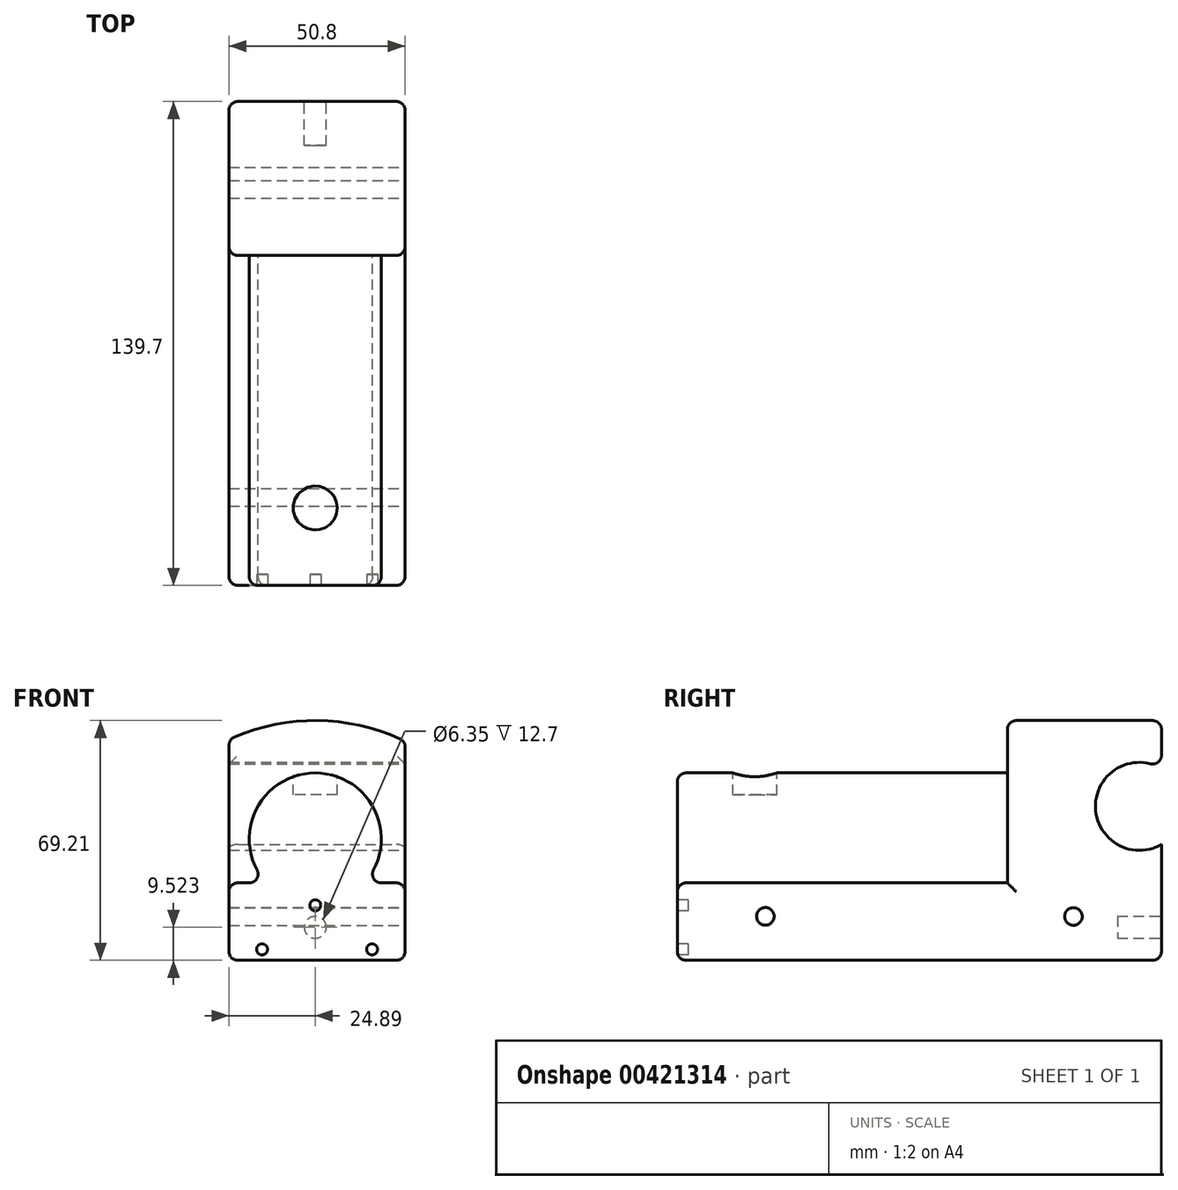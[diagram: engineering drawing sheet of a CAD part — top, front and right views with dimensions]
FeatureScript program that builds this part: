
annotation { "Feature Type Name" : "Feature", "Feature Type Description" : "" }
export const myFeature = defineFeature(function(context is Context, id is Id, definition is map)
    precondition{}
    {
        {
            var Q0;
            Q0=qCreatedBy(makeId("Front.planeOp"),FACE);
            var sketch = newSketch(context, id + "F0", { "sketchPlane" : qUnion([Q0])});
            skLineSegment(sketch, "E0.bottom", {"start": v(-24.89, 0) * mm, "end": v(-14.2, 0) * mm});
            skLineSegment(sketch, "E0.top", {"start": v(-24.89, -22.35) * mm, "end": v(25.91, -22.35) * mm});
            skLineSegment(sketch, "E0.left", {"start": v(-24.89, 0) * mm, "end": v(-24.89, -22.35) * mm});
            skLineSegment(sketch, "E0.right", {"start": v(25.91, 0) * mm, "end": v(25.91, -22.35) * mm});
            skArc(sketch, "E1", {"start": v(14.2, 0) * mm, "mid": v(0, 31.75) * mm, "end": v(-14.2, 0) * mm});
            skLineSegment(sketch, "E2.trimOffspring", {"start": v(14.2, 0) * mm, "end": v(25.91, 0) * mm});
            skSolve(sketch);
        }
        {
            var Q0;
            Q0=makeQuery(id+"F0.imprint","IMPRINT",FACE,{"disambiguationData":[TD([[makeQuery(id+"F0.imprint","IMPRINT",EDGE,{"derivedFrom":sQuery(id+"F0.wireOp",EDGE,"E0.bottom")}),-1.0]])]});
            extrude(context, id + "F1", {"entities" : qUnion([Q0]), "depth" : 95.25 * mm});
        }
        {
            var Q0;
            Q0=makeQuery(id+"F1.opExtrude","CAP_FACE",FACE,{"disambiguationData":[OSD([sQuery(id+"F0.wireOp",EDGE,"E0.bottom"),sQuery(id+"F0.wireOp",EDGE,"E0.top"),sQuery(id+"F0.wireOp",EDGE,"E0.left"),sQuery(id+"F0.wireOp",EDGE,"E0.right"),sQuery(id+"F0.wireOp",EDGE,"E1"),sQuery(id+"F0.wireOp",EDGE,"E2.trimOffspring")])],"isStart":true});
            var sketch = newSketch(context, id + "F2", { "sketchPlane" : qUnion([Q0])});
            skArc(sketch, "E3", {"start": v(24.89, 41.43) * mm, "mid": v(-0.57, 46.86) * mm, "end": v(-25.91, 40.95) * mm});
            skLineSegment(sketch, "E4", {"start": v(-25.91, 0) * mm, "end": v(-25.91, 40.95) * mm});
            skLineSegment(sketch, "E5", {"start": v(-25.91, 40.95) * mm, "end": v(-25.91, 40.95) * mm});
            skLineSegment(sketch, "E6", {"start": v(24.89, 0) * mm, "end": v(24.89, 41.43) * mm});
            skSolve(sketch);
        }
        {
            var Q0;
            Q0=makeQuery(id+"F2.imprint","IMPRINT",FACE,{"disambiguationData":[TD([[makeQuery(id+"F2.imprint","IMPRINT",EDGE,{"derivedFrom":sQuery(id+"F2.wireOp",EDGE,"E3")}),1.0]])]});
            var Q1;
            Q1=makeQuery(id+"F2.imprint","IMPRINT",FACE,{"disambiguationData":[TD([[makeQuery(id+"F2.imprint","IMPRINT",EDGE,{"derivedFrom":makeQuery(id+"F1.opExtrude","CAP_EDGE",EDGE,{"disambiguationData":[OSD([sQuery(id+"F0.wireOp",EDGE,"E0.bottom")])],"isStart":true})}),1.0]])]});
            extrude(context, id + "F3", {"entities" : qUnion([Q0, Q1]), "operationType" : NewBodyOperationType.ADD, "depth" : 44.45 * mm});
        }
        {
            var Q0;
            {var subQ0=sQuery(id+"F0.wireOp",EDGE,"E0.right");Q0=makeQuery(id+"F3.boolean.opBoolean","MERGE",FACE,{"derivedFrom":[makeQuery(id+"F1.opExtrude","SWEPT_FACE",FACE,{"disambiguationData":[OSD([subQ0])]}),makeQuery(id+"F3.opExtrude","SWEPT_FACE",FACE,{"disambiguationData":[OSD([subQ0,sQuery(id+"F2.wireOp",EDGE,"E4")])]})]});}
            var sketch = newSketch(context, id + "F4", { "sketchPlane" : qUnion([Q0])});
            skArc(sketch, "E7", {"start": v(44.45, 33.1) * mm, "mid": v(25.4, 22.1) * mm, "end": v(44.45, 11.1) * mm});
            skLineSegment(sketch, "E8", {"start": v(44.45, 33.1) * mm, "end": v(44.45, 11.1) * mm});
            skPoint(sketch, "E8.endSnap0", {"position": v(44.45, 9.3) * mm});
            skSolve(sketch);
        }
        {
            var Q0;
            Q0=makeQuery(id+"F4.imprint","IMPRINT",FACE,{"disambiguationData":[TD([[makeQuery(id+"F4.imprint","IMPRINT",EDGE,{"derivedFrom":sQuery(id+"F4.wireOp",EDGE,"E7")}),1.0]])]});
            extrude(context, id + "F5", {"entities" : qUnion([Q0]), "operationType" : NewBodyOperationType.REMOVE, "oppositeDirection" : true, "depth" : 50.8 * mm});
        }
        {
            var Q0;
            Q0=makeQuery(id+"F1.opExtrude","CAP_FACE",FACE,{"disambiguationData":[OSD([sQuery(id+"F0.wireOp",EDGE,"E0.bottom"),sQuery(id+"F0.wireOp",EDGE,"E0.top"),sQuery(id+"F0.wireOp",EDGE,"E0.left"),sQuery(id+"F0.wireOp",EDGE,"E0.right"),sQuery(id+"F0.wireOp",EDGE,"E1"),sQuery(id+"F0.wireOp",EDGE,"E2.trimOffspring")])],"isStart":false});
            var sketch = newSketch(context, id + "F6", { "sketchPlane" : qUnion([Q0])});
            skCircle(sketch, "E9", {"center": v(-15.36, -19.18) * mm, "radius": 1.59 * mm});
            skCircle(sketch, "E10", {"center": v(0, -6.48) * mm, "radius": 1.59 * mm});
            skCircle(sketch, "E11", {"center": v(16.39, -19.18) * mm, "radius": 1.59 * mm});
            skLineSegment(sketch, "E12.0", {"start": v(-24.89, -22.35) * mm, "end": v(25.91, -22.35) * mm});
            skSolve(sketch);
        }
        {
            var Q0;
            Q0=makeQuery(id+"F6.imprint","IMPRINT",FACE,{"disambiguationData":[TD([[makeQuery(id+"F6.imprint","IMPRINT",EDGE,{"derivedFrom":sQuery(id+"F6.wireOp",EDGE,"E10")}),1.0]])]});
            var Q1;
            Q1=makeQuery(id+"F6.imprint","IMPRINT",FACE,{"disambiguationData":[TD([[makeQuery(id+"F6.imprint","IMPRINT",EDGE,{"derivedFrom":sQuery(id+"F6.wireOp",EDGE,"E9")}),1.0]])]});
            var Q2;
            Q2=makeQuery(id+"F6.imprint","IMPRINT",FACE,{"disambiguationData":[TD([[makeQuery(id+"F6.imprint","IMPRINT",EDGE,{"derivedFrom":sQuery(id+"F6.wireOp",EDGE,"E11")}),1.0]])]});
            extrude(context, id + "F7", {"entities" : qUnion([Q0, Q1, Q2]), "operationType" : NewBodyOperationType.REMOVE, "oppositeDirection" : true, "depth" : 3.17 * mm});
        }
        {
            var Q0;
            {var subQ0=sQuery(id+"F0.wireOp",EDGE,"E0.right");Q0=makeQuery(id+"F3.boolean.opBoolean","MERGE",FACE,{"derivedFrom":[makeQuery(id+"F1.opExtrude","SWEPT_FACE",FACE,{"disambiguationData":[OSD([subQ0])]}),makeQuery(id+"F3.opExtrude","SWEPT_FACE",FACE,{"disambiguationData":[OSD([subQ0,sQuery(id+"F2.wireOp",EDGE,"E4")])]})]});}
            var sketch = newSketch(context, id + "F8", { "sketchPlane" : qUnion([Q0])});
            skPoint(sketch, "E13", {"position": v(-69.85, -9.65) * mm});
            skPoint(sketch, "E14", {"position": v(19.05, -9.7) * mm});
            skSolve(sketch);
        }
        {
            var Q0;
            Q0=sQuery(id+"F8.wireOp",VERTEX,"E13");
            var Q1;
            Q1=sQuery(id+"F8.wireOp",VERTEX,"E14");
            var Q2;
            Q2=makeQuery(id+"F1.opExtrude","SWEPT_BODY",BODY,{"disambiguationData":[OSD([sQuery(id+"F0.wireOp",EDGE,"E0.bottom"),sQuery(id+"F0.wireOp",EDGE,"E0.top"),sQuery(id+"F0.wireOp",EDGE,"E0.left"),sQuery(id+"F0.wireOp",EDGE,"E0.right"),sQuery(id+"F0.wireOp",EDGE,"E1"),sQuery(id+"F0.wireOp",EDGE,"E2.trimOffspring")])]});
            hole(context, id + "F9", {"style" : HoleStyle.SIMPLE, "endStyle" : HoleEndStyle.THROUGH, "standardTappedOrClearance" : lookupTablePath({ "standard" : "ANSI", "fit" : "Normal (ASME)", "engagement" : "75%", "pitch" : "20 tpi", "size" : "1/4", "type" : "Tapped" }), "standardBlindInLast" : lookupTablePath({ "fit" : "Free", "standard" : "ANSI", "engagement" : "75%", "pitch" : "20 tpi", "size" : "1/4", "type" : "Tapped" }), "holeDiameter" : 5.1 * mm, "showTappedDepth" : true, "tappedDepth" : 50.8 * mm, "tapClearance" : 3, "locations" : qUnion([Q0, Q1]), "scope" : qUnion([Q2]), "majorDiameter" : 6.35 * mm});
        }
        {
            var Q0;
            Q0=qCreatedBy(makeId("Top.planeOp"),FACE);
            cPlane(context, id + "F10", {"entities" : qUnion([Q0]), "cplaneType" : CPlaneType.OFFSET, "offset" : 31.75 * mm, "width" : 152.4 * mm, "height" : 152.4 * mm});
        }
        {
            var Q0;
            Q0=qCreatedBy(id+"F10.planeOp",FACE);
            var sketch = newSketch(context, id + "F11", { "sketchPlane" : qUnion([Q0])});
            skCircle(sketch, "E15", {"center": v(0, -72.9) * mm, "radius": 6.35 * mm});
            skSolve(sketch);
        }
        {
            var Q0;
            Q0=makeQuery(id+"F11.imprint","IMPRINT",FACE,{"disambiguationData":[TD([[makeQuery(id+"F11.imprint","IMPRINT",EDGE,{"derivedFrom":sQuery(id+"F11.wireOp",EDGE,"E15")}),1.0]])]});
            extrude(context, id + "F12", {"entities" : qUnion([Q0]), "operationType" : NewBodyOperationType.REMOVE, "oppositeDirection" : true, "depth" : 6.35 * mm});
        }
        {
            var Q0;
            {var subQ0=sQuery(id+"F2.wireOp",EDGE,"E4");var subQ1=sQuery(id+"F0.wireOp",EDGE,"E0.right");var subQ2=sQuery(id+"F0.wireOp",EDGE,"E0.left");var subQ3=sQuery(id+"F2.wireOp",EDGE,"E6");var subQ4=sQuery(id+"F0.wireOp",EDGE,"E0.top");Q0=makeQuery(id+"F5.boolean.opBoolean","SPLIT",FACE,{"disambiguationData":[TD([makeQuery(id+"F1.opExtrude","SWEPT_FACE",FACE,{"disambiguationData":[OSD([subQ4])]})])],"derivedFrom":makeQuery(id+"F3.opExtrude","CAP_FACE",FACE,{"disambiguationData":[OSD([subQ4,subQ2,subQ1,sQuery(id+"F2.wireOp",EDGE,"E3"),subQ0,subQ3])],"isStart":false})});}
            var sketch = newSketch(context, id + "F13", { "sketchPlane" : qUnion([Q0])});
            skCircle(sketch, "E16", {"center": v(0, -12.83) * mm, "radius": 3.18 * mm});
            skSolve(sketch);
        }
        {
            var Q0;
            Q0=makeQuery(id+"F13.imprint","IMPRINT",FACE,{"disambiguationData":[TD([[makeQuery(id+"F13.imprint","IMPRINT",EDGE,{"derivedFrom":sQuery(id+"F13.wireOp",EDGE,"E16")}),1.0]])]});
            extrude(context, id + "F14", {"entities" : qUnion([Q0]), "operationType" : NewBodyOperationType.REMOVE, "oppositeDirection" : true, "offsetDistance" : 25.4 * mm, "depth" : 12.7 * mm});
        }
        {
            var Q0;
            {var subQ0=sQuery(id+"F2.wireOp",EDGE,"E4");var subQ1=sQuery(id+"F0.wireOp",EDGE,"E0.right");var subQ2=sQuery(id+"F0.wireOp",EDGE,"E0.left");var subQ3=sQuery(id+"F2.wireOp",EDGE,"E3");var subQ4=sQuery(id+"F2.wireOp",EDGE,"E6");Q0=makeQuery(id+"F5.boolean.opBoolean","SPLIT",FACE,{"disambiguationData":[TD([makeQuery(id+"F3.opExtrude","SWEPT_FACE",FACE,{"disambiguationData":[OSD([subQ3])]})])],"derivedFrom":makeQuery(id+"F3.opExtrude","CAP_FACE",FACE,{"disambiguationData":[OSD([sQuery(id+"F0.wireOp",EDGE,"E0.top"),subQ2,subQ1,subQ3,subQ0,subQ4])],"isStart":false})});}
            var Q1;
            Q1=makeQuery(id+"F3.opExtrude","SWEPT_FACE",FACE,{"disambiguationData":[OSD([sQuery(id+"F2.wireOp",EDGE,"E3")])]});
            var Q2;
            Q2=makeQuery(id+"F5.boolean.opBoolean","COPY",EDGE,{"derivedFrom":makeQuery(id+"F5.opExtrude","CAP_EDGE",EDGE,{"disambiguationData":[OSD([sQuery(id+"F4.wireOp",EDGE,"E7")])],"isStart":false})});
            var Q3;
            Q3=makeQuery(id+"F3.opExtrude","CAP_EDGE",EDGE,{"disambiguationData":[OSD([sQuery(id+"F0.wireOp",EDGE,"E0.left"),sQuery(id+"F2.wireOp",EDGE,"E6")])],"isStart":true});
            var Q4;
            Q4=makeQuery(id+"F1.opExtrude","SWEPT_EDGE",EDGE,{"disambiguationData":[OSD([sQuery(id+"F0.wireOp",EDGE,"E0.bottom"),sQuery(id+"F0.wireOp",EDGE,"E0.left")])]});
            var Q5;
            {var subQ0=sQuery(id+"F0.wireOp",EDGE,"E0.left");var subQ1=sQuery(id+"F0.wireOp",EDGE,"E0.top");Q5=makeQuery(id+"F3.boolean.opBoolean","MERGE",EDGE,{"derivedFrom":[makeQuery(id+"F1.opExtrude","SWEPT_EDGE",EDGE,{"disambiguationData":[OSD([subQ1,subQ0])]}),makeQuery(id+"F3.opExtrude","SWEPT_EDGE",EDGE,{"disambiguationData":[OSD([subQ1,subQ0])]})]});}
            var Q6;
            {var subQ0=sQuery(id+"F2.wireOp",EDGE,"E6");var subQ1=sQuery(id+"F0.wireOp",EDGE,"E0.left");var subQ2=sQuery(id+"F0.wireOp",EDGE,"E0.top");Q6=makeQuery(id+"F5.boolean.opBoolean","SPLIT",EDGE,{"disambiguationData":[TD([makeQuery(id+"F1.opExtrude","SWEPT_FACE",FACE,{"disambiguationData":[OSD([subQ2])]})])],"derivedFrom":makeQuery(id+"F3.opExtrude","CAP_EDGE",EDGE,{"disambiguationData":[OSD([subQ1,subQ0])],"isStart":false})});}
            var Q7;
            {var subQ0=sQuery(id+"F4.wireOp",EDGE,"E8");var subQ1=sQuery(id+"F4.wireOp",EDGE,"E7");var subQ2=sQuery(id+"F2.wireOp",EDGE,"E4");var subQ3=sQuery(id+"F0.wireOp",EDGE,"E0.right");Q7=makeQuery(id+"F5.boolean.opBoolean","COPY",EDGE,{"derivedFrom":makeQuery(id+"F5.opExtrude","SWEPT_EDGE",EDGE,{"disambiguationData":[OSD([subQ3,subQ2,subQ1,subQ0]),TDD([makeQuery(id+"F4.imprint","INTERSECT",VERTEX,{"disambiguationData":[OD(1.0)],"derivedFrom":[makeQuery(id+"F3.opExtrude","CAP_EDGE",EDGE,{"disambiguationData":[OSD([subQ3,subQ2])],"isStart":false}),subQ1,subQ0]})])]})});}
            var Q8;
            {var subQ0=sQuery(id+"F2.wireOp",EDGE,"E4");var subQ1=sQuery(id+"F0.wireOp",EDGE,"E0.right");var subQ2=sQuery(id+"F0.wireOp",EDGE,"E0.top");Q8=makeQuery(id+"F5.boolean.opBoolean","SPLIT",EDGE,{"disambiguationData":[TD([makeQuery(id+"F1.opExtrude","SWEPT_FACE",FACE,{"disambiguationData":[OSD([subQ2])]})])],"derivedFrom":makeQuery(id+"F3.opExtrude","CAP_EDGE",EDGE,{"disambiguationData":[OSD([subQ1,subQ0])],"isStart":false})});}
            var Q9;
            Q9=makeQuery(id+"F3.opExtrude","CAP_EDGE",EDGE,{"disambiguationData":[OSD([sQuery(id+"F0.wireOp",EDGE,"E0.top")])],"isStart":false});
            var Q10;
            Q10=makeQuery(id+"F3.opExtrude","CAP_EDGE",EDGE,{"disambiguationData":[OSD([sQuery(id+"F0.wireOp",EDGE,"E0.right"),sQuery(id+"F2.wireOp",EDGE,"E4")])],"isStart":true});
            var Q11;
            Q11=makeQuery(id+"F1.opExtrude","SWEPT_EDGE",EDGE,{"disambiguationData":[OSD([sQuery(id+"F0.wireOp",EDGE,"E0.right"),sQuery(id+"F0.wireOp",EDGE,"E2.trimOffspring")])]});
            var Q12;
            Q12=makeQuery(id+"F1.opExtrude","CAP_EDGE",EDGE,{"disambiguationData":[OSD([sQuery(id+"F0.wireOp",EDGE,"E0.right")])],"isStart":false});
            var Q13;
            {var subQ0=sQuery(id+"F0.wireOp",EDGE,"E0.right");var subQ1=sQuery(id+"F0.wireOp",EDGE,"E0.top");Q13=makeQuery(id+"F3.boolean.opBoolean","MERGE",EDGE,{"derivedFrom":[makeQuery(id+"F1.opExtrude","SWEPT_EDGE",EDGE,{"disambiguationData":[OSD([subQ1,subQ0])]}),makeQuery(id+"F3.opExtrude","SWEPT_EDGE",EDGE,{"disambiguationData":[OSD([subQ1,subQ0])]})]});}
            var Q14;
            Q14=makeQuery(id+"F1.opExtrude","CAP_EDGE",EDGE,{"disambiguationData":[OSD([sQuery(id+"F0.wireOp",EDGE,"E1")])],"isStart":false});
            var Q15;
            Q15=makeQuery(id+"F1.opExtrude","CAP_EDGE",EDGE,{"disambiguationData":[OSD([sQuery(id+"F0.wireOp",EDGE,"E2.trimOffspring")])],"isStart":false});
            var Q16;
            Q16=makeQuery(id+"F1.opExtrude","CAP_EDGE",EDGE,{"disambiguationData":[OSD([sQuery(id+"F0.wireOp",EDGE,"E0.bottom")])],"isStart":false});
            var Q17;
            Q17=makeQuery(id+"F1.opExtrude","CAP_EDGE",EDGE,{"disambiguationData":[OSD([sQuery(id+"F0.wireOp",EDGE,"E0.left")])],"isStart":false});
            var Q18;
            Q18=makeQuery(id+"F1.opExtrude","CAP_EDGE",EDGE,{"disambiguationData":[OSD([sQuery(id+"F0.wireOp",EDGE,"E0.top")])],"isStart":false});
            var Q19;
            Q19=makeQuery(id+"F1.opExtrude","SWEPT_EDGE",EDGE,{"disambiguationData":[OSD([sQuery(id+"F0.wireOp",EDGE,"E1"),sQuery(id+"F0.wireOp",EDGE,"E2.trimOffspring")])]});
            var Q20;
            Q20=makeQuery(id+"F1.opExtrude","SWEPT_EDGE",EDGE,{"disambiguationData":[OSD([sQuery(id+"F0.wireOp",EDGE,"E0.bottom"),sQuery(id+"F0.wireOp",EDGE,"E1")])]});
            var Q21;
            Q21=makeQuery(id+"F5.boolean.opBoolean","COPY",EDGE,{"derivedFrom":makeQuery(id+"F5.opExtrude","CAP_EDGE",EDGE,{"disambiguationData":[OSD([sQuery(id+"F4.wireOp",EDGE,"E7")])],"isStart":true})});
            var Q22;
            Q22=makeQuery(id+"F1.opExtrude","CAP_EDGE",EDGE,{"disambiguationData":[OSD([sQuery(id+"F0.wireOp",EDGE,"E1")])],"isStart":true});
            fillet(context, id + "F15", {"entities" : qUnion([Q0, Q1, Q2, Q3, Q4, Q5, Q6, Q7, Q8, Q9, Q10, Q11, Q12, Q13, Q14, Q15, Q16, Q17, Q18, Q19, Q20, Q21, Q22]), "radius" : 2.54 * mm, "tangentPropagation" : true, "allowEdgeOverflow" : false});
        }
    });
